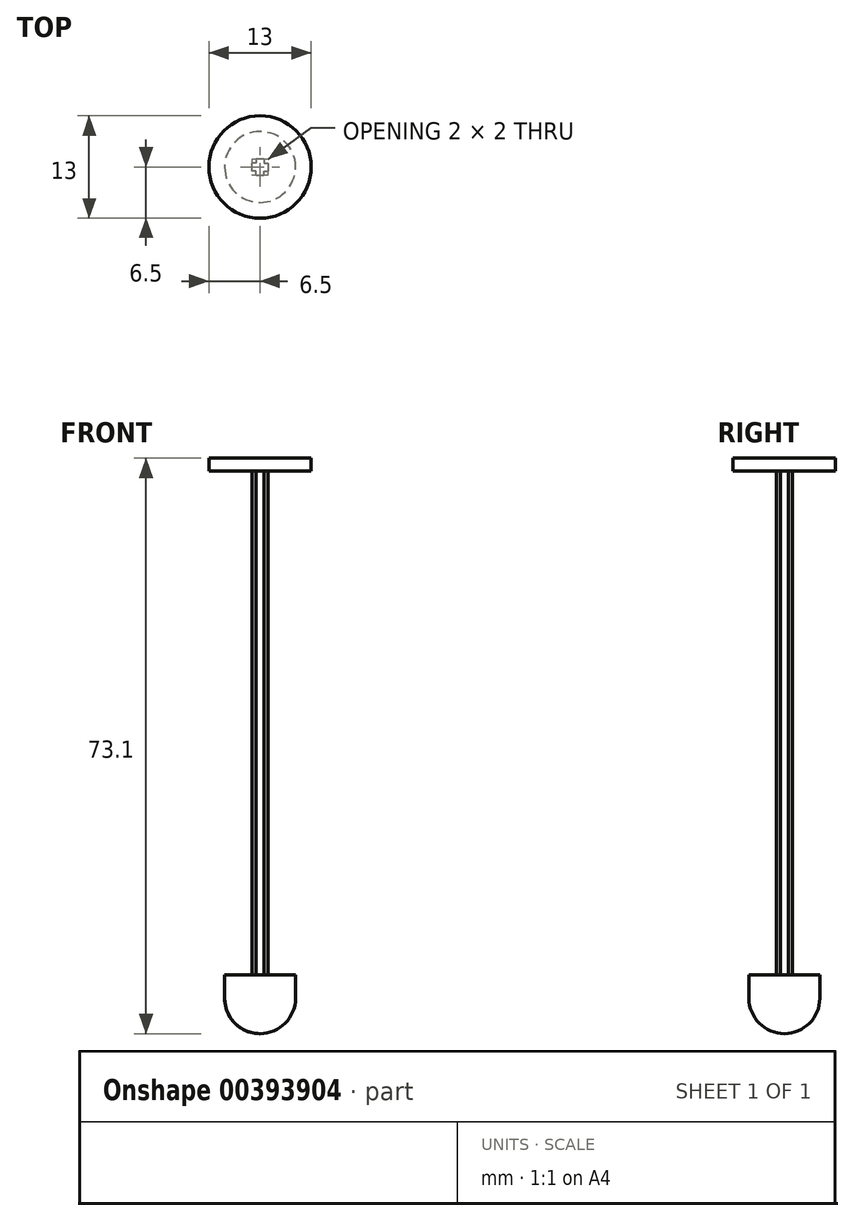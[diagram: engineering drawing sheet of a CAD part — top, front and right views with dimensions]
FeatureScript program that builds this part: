
annotation { "Feature Type Name" : "Feature", "Feature Type Description" : "" }
export const myFeature = defineFeature(function(context is Context, id is Id, definition is map)
    precondition{}
    {
        {
            var Q0;
            Q0=qCreatedBy(makeId("Top.planeOp"),FACE);
            var sketch = newSketch(context, id + "F0", { "sketchPlane" : qUnion([Q0])});
            skCircle(sketch, "E0", {"center": v(0, 0) * mm, "radius": 6.5 * mm});
            skSolve(sketch);
        }
        {
            var Q0;
            Q0=makeQuery(id+"F0.imprint","IMPRINT",FACE,{"disambiguationData":[TD([[makeQuery(id+"F0.imprint","IMPRINT",EDGE,{"derivedFrom":sQuery(id+"F0.wireOp",EDGE,"E0")}),1.0]])]});
            extrude(context, id + "F1", {"entities" : qUnion([Q0]), "depth" : 1.6 * mm, "offsetDistance" : 25 * mm});
        }
        {
            var Q0;
            Q0=makeQuery(id+"F1.opExtrude","CAP_FACE",FACE,{"disambiguationData":[OSD([sQuery(id+"F0.wireOp",EDGE,"E0")])],"isStart":true});
            var sketch = newSketch(context, id + "F2", { "sketchPlane" : qUnion([Q0])});
            skLineSegment(sketch, "E1", {"start": v(0, 1) * mm, "end": v(0.5, 1) * mm});
            skLineSegment(sketch, "E2", {"start": v(0.5, 1) * mm, "end": v(0.5, 0.5) * mm});
            skLineSegment(sketch, "E3", {"start": v(0.5, 0.5) * mm, "end": v(1, 0.5) * mm});
            skLineSegment(sketch, "E4", {"start": v(1, 0.5) * mm, "end": v(1, 0) * mm});
            skLineSegment(sketch, "E5.MirrorCS", {"start": v(-1, 0.5) * mm, "end": v(-1, 0) * mm});
            skLineSegment(sketch, "E6.MirrorCS", {"start": v(-0.5, 0.5) * mm, "end": v(-1, 0.5) * mm});
            skLineSegment(sketch, "E7.MirrorCS", {"start": v(-0.5, 1) * mm, "end": v(-0.5, 0.5) * mm});
            skLineSegment(sketch, "E8.MirrorCS", {"start": v(0, 1) * mm, "end": v(-0.5, 1) * mm});
            skLineSegment(sketch, "E9.MirrorCS", {"start": v(0, -1) * mm, "end": v(0.5, -1) * mm});
            skLineSegment(sketch, "E10.MirrorCS", {"start": v(0, -1) * mm, "end": v(-0.5, -1) * mm});
            skLineSegment(sketch, "E11.MirrorCS", {"start": v(0.5, -1) * mm, "end": v(0.5, -0.5) * mm});
            skLineSegment(sketch, "E12.MirrorCS", {"start": v(0.5, -0.5) * mm, "end": v(1, -0.5) * mm});
            skLineSegment(sketch, "E13.MirrorCS", {"start": v(1, -0.5) * mm, "end": v(1, 0) * mm});
            skLineSegment(sketch, "E14.MirrorCS", {"start": v(-1, -0.5) * mm, "end": v(-1, 0) * mm});
            skLineSegment(sketch, "E15.MirrorCS", {"start": v(-0.5, -1) * mm, "end": v(-0.5, -0.5) * mm});
            skLineSegment(sketch, "E16.MirrorCS", {"start": v(-0.5, -0.5) * mm, "end": v(-1, -0.5) * mm});
            skSolve(sketch);
        }
        {
            var Q0;
            Q0=makeQuery(id+"F2.imprint","IMPRINT",FACE,{"disambiguationData":[TD([[makeQuery(id+"F2.imprint","IMPRINT",EDGE,{"derivedFrom":sQuery(id+"F2.wireOp",EDGE,"E1")}),-1.0]])]});
            extrude(context, id + "F3", {"entities" : qUnion([Q0]), "operationType" : NewBodyOperationType.ADD, "depth" : 64 * mm, "offsetDistance" : 25 * mm});
        }
        {
            var Q0;
            Q0=makeQuery(id+"F3.opExtrude","CAP_FACE",FACE,{"disambiguationData":[OSD([sQuery(id+"F2.wireOp",EDGE,"E1"),sQuery(id+"F2.wireOp",EDGE,"E2"),sQuery(id+"F2.wireOp",EDGE,"E3"),sQuery(id+"F2.wireOp",EDGE,"E4"),sQuery(id+"F2.wireOp",EDGE,"E5.MirrorCS"),sQuery(id+"F2.wireOp",EDGE,"E6.MirrorCS"),sQuery(id+"F2.wireOp",EDGE,"E7.MirrorCS"),sQuery(id+"F2.wireOp",EDGE,"E8.MirrorCS"),sQuery(id+"F2.wireOp",EDGE,"E9.MirrorCS"),sQuery(id+"F2.wireOp",EDGE,"E10.MirrorCS"),sQuery(id+"F2.wireOp",EDGE,"E11.MirrorCS"),sQuery(id+"F2.wireOp",EDGE,"E12.MirrorCS"),sQuery(id+"F2.wireOp",EDGE,"E13.MirrorCS"),sQuery(id+"F2.wireOp",EDGE,"E14.MirrorCS"),sQuery(id+"F2.wireOp",EDGE,"E15.MirrorCS"),sQuery(id+"F2.wireOp",EDGE,"E16.MirrorCS")])],"isStart":false});
            var sketch = newSketch(context, id + "F4", { "sketchPlane" : qUnion([Q0])});
            skCircle(sketch, "E17", {"center": v(0, 0) * mm, "radius": 4.5 * mm});
            skSolve(sketch);
        }
        {
            var Q0;
            Q0=makeQuery(id+"F4.imprint","IMPRINT",FACE,{"disambiguationData":[TD([[makeQuery(id+"F4.imprint","IMPRINT",EDGE,{"derivedFrom":sQuery(id+"F4.wireOp",EDGE,"E17")}),1.0]])]});
            var Q1;
            Q1=makeQuery(id+"F4.imprint","IMPRINT",FACE,{"disambiguationData":[TD([[makeQuery(id+"F4.imprint","IMPRINT",EDGE,{"derivedFrom":makeQuery(id+"F3.opExtrude","CAP_EDGE",EDGE,{"disambiguationData":[OSD([sQuery(id+"F2.wireOp",EDGE,"E2")])],"isStart":false})}),-1.0]])]});
            extrude(context, id + "F5", {"entities" : qUnion([Q0, Q1]), "operationType" : NewBodyOperationType.ADD, "depth" : 7.5 * mm, "offsetDistance" : 25 * mm});
        }
        {
            var Q0;
            Q0=makeQuery(id+"F5.opExtrude","CAP_FACE",FACE,{"disambiguationData":[OSD([sQuery(id+"F4.wireOp",EDGE,"E17")])],"isStart":false});
            fillet(context, id + "F6", {"entities" : qUnion([Q0]), "radius" : 4.5 * mm, "tangentPropagation" : true, "allowEdgeOverflow" : false});
        }
    });
